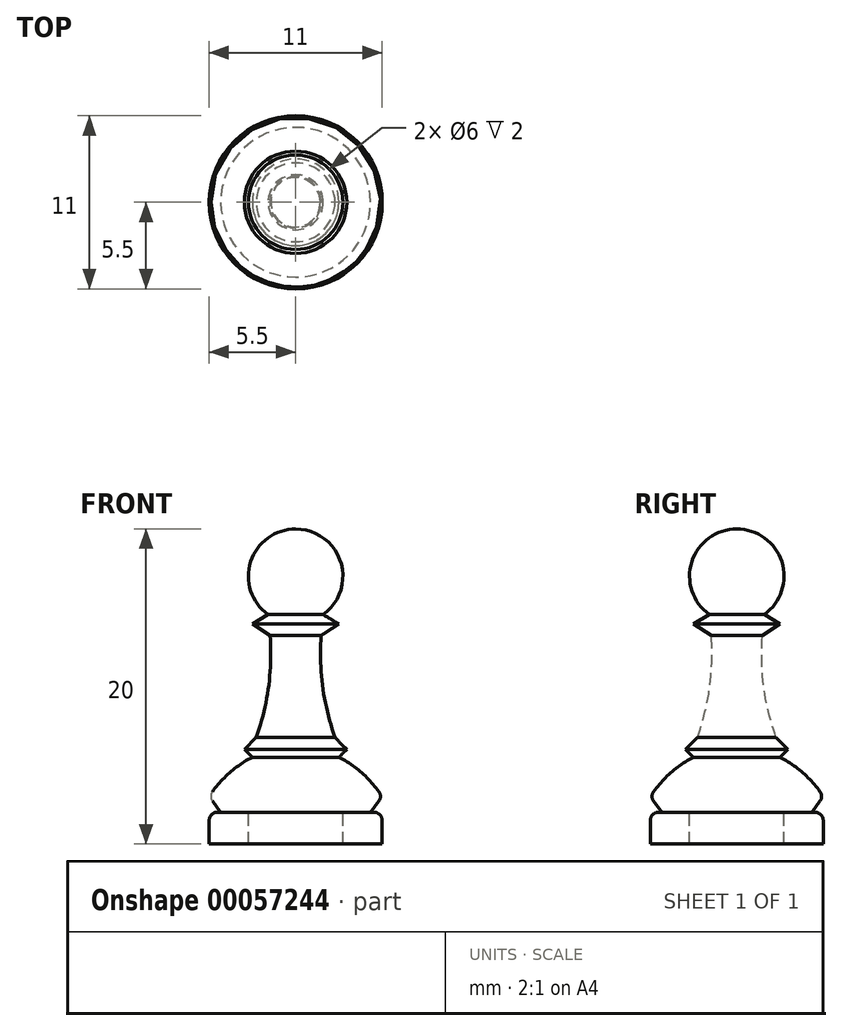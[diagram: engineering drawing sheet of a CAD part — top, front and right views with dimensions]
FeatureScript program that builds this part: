
annotation { "Feature Type Name" : "Feature", "Feature Type Description" : "" }
export const myFeature = defineFeature(function(context is Context, id is Id, definition is map)
    precondition{}
    {
        {
            var Q0;
            Q0=qCreatedBy(makeId("Front.planeOp"),FACE);
            var sketch = newSketch(context, id + "F0", { "sketchPlane" : qUnion([Q0])});
            skLineSegment(sketch, "E0", {"start": v(0, 0) * mm, "end": v(0, 20) * mm, "construction": true});
            skLineSegment(sketch, "E1", {"start": v(0, 20) * mm, "end": v(-2.87, 20) * mm, "construction": true});
            skArc(sketch, "E2", {"start": v(1.75, 14.56) * mm, "mid": v(2.86, 17.92) * mm, "end": v(0, 20) * mm});
            skLineSegment(sketch, "E3", {"start": v(1.75, 14.56) * mm, "end": v(2.75, 13.96) * mm});
            skLineSegment(sketch, "E4", {"start": v(2.75, 13.96) * mm, "end": v(1.63, 13.25) * mm});
            skArc(sketch, "E5", {"start": v(1.63, 13.25) * mm, "mid": v(1.72, 9.95) * mm, "end": v(2.5, 6.75) * mm});
            skLineSegment(sketch, "E6", {"start": v(2.5, 6.75) * mm, "end": v(3.25, 6) * mm});
            skLineSegment(sketch, "E7", {"start": v(3.25, 6) * mm, "end": v(2.75, 5.5) * mm});
            skArc(sketch, "E8", {"start": v(5.5, 3) * mm, "mid": v(4.29, 4.43) * mm, "end": v(2.75, 5.5) * mm});
            skLineSegment(sketch, "E9", {"start": v(5.5, 3) * mm, "end": v(4.76, 2) * mm});
            skLineSegment(sketch, "E10", {"start": v(4.76, 2) * mm, "end": v(5.48, 2) * mm});
            skLineSegment(sketch, "E11", {"start": v(5.48, 2) * mm, "end": v(5.5, 0) * mm});
            skLineSegment(sketch, "E12", {"start": v(5.5, 0) * mm, "end": v(3, 0) * mm});
            skLineSegment(sketch, "E13", {"start": v(0, 20) * mm, "end": v(0, 2) * mm});
            skLineSegment(sketch, "E14", {"start": v(0, 28.83) * mm, "end": v(0, -16.82) * mm, "construction": true});
            skLineSegment(sketch, "E15", {"start": v(3, 0) * mm, "end": v(3, 2) * mm});
            skLineSegment(sketch, "E16", {"start": v(3, 2) * mm, "end": v(0, 2) * mm});
            skSolve(sketch);
        }
        {
            var Q0;
            Q0 = qSketchRegion(id + "F0", true);
            var Q1;
            Q1=sQuery(id+"F0.wireOp",EDGE,"E14");
            revolve(context, id + "F1", {"entities" : qUnion([Q0]), "axis" : qUnion([Q1]), "revolveType" : RevolveType.FULL});
        }
        {
            var Q0;
            Q0=makeQuery(id+"F1.opRevolve","SWEPT_EDGE",EDGE,{"disambiguationData":[OSD([sQuery(id+"F0.wireOp",EDGE,"E8"),sQuery(id+"F0.wireOp",EDGE,"E9")])]});
            var Q1;
            Q1=makeQuery(id+"F1.opRevolve","SWEPT_EDGE",EDGE,{"disambiguationData":[OSD([sQuery(id+"F0.wireOp",EDGE,"E10"),sQuery(id+"F0.wireOp",EDGE,"E11")])]});
            fillet(context, id + "F2", {"entities" : qUnion([Q0, Q1]), "radius" : .5 * mm, "tangentPropagation" : true, "allowEdgeOverflow" : false});
        }
    });
